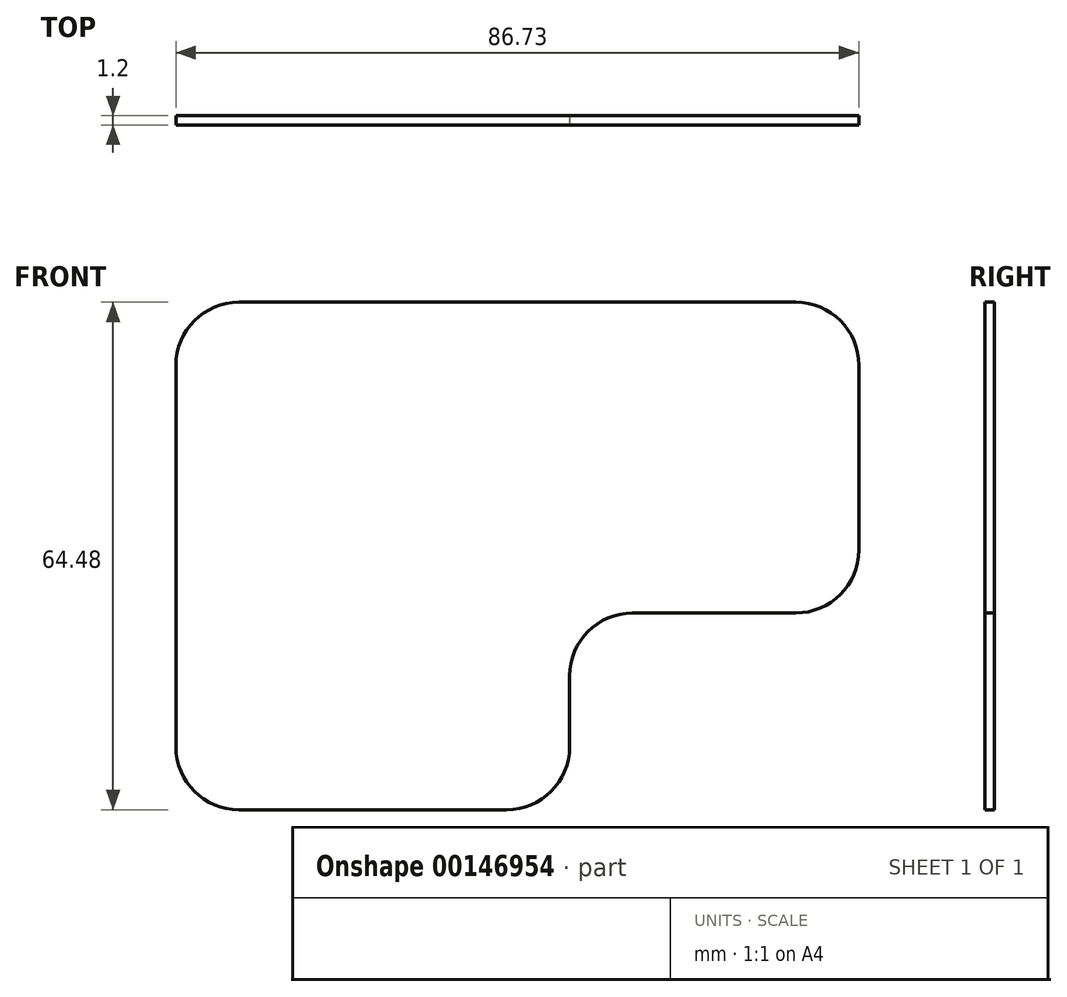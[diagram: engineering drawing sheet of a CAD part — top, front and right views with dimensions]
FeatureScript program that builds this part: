
annotation { "Feature Type Name" : "Feature", "Feature Type Description" : "" }
export const myFeature = defineFeature(function(context is Context, id is Id, definition is map)
    precondition{}
    {
        {
            var Q0;
            Q0=qCreatedBy(makeId("Front.planeOp"),FACE);
            var sketch = newSketch(context, id + "F0", { "sketchPlane" : qUnion([Q0])});
            skLineSegment(sketch, "E0", {"start": v(0, 0) * mm, "end": v(0, 50) * mm, "construction": true});
            skLineSegment(sketch, "E1", {"start": v(0, 50) * mm, "end": v(75, 50) * mm, "construction": true});
            skLineSegment(sketch, "E2", {"start": v(0, 0) * mm, "end": v(30.27, 0) * mm});
            skLineSegment(sketch, "E3", {"start": v(38.27, 8) * mm, "end": v(38.27, 17) * mm});
            skLineSegment(sketch, "E4", {"start": v(46.27, 25) * mm, "end": v(67, 25) * mm});
            skLineSegment(sketch, "E5", {"start": v(75, 33) * mm, "end": v(75, 50) * mm});
            skLineSegment(sketch, "E6", {"start": v(0, 0) * mm, "end": v(-3.73, 0) * mm});
            skLineSegment(sketch, "E7", {"start": v(-11.73, 8) * mm, "end": v(-11.73, 56.48) * mm});
            skLineSegment(sketch, "E8", {"start": v(-3.73, 64.48) * mm, "end": v(67, 64.48) * mm});
            skLineSegment(sketch, "E9", {"start": v(75, 56.48) * mm, "end": v(75, 50) * mm});
            skPoint(sketch, "E10.visualSharp", {"position": v(-11.73, 0) * mm});
            skArc(sketch, "E10.filletArc", {"start": v(-11.73, 8) * mm, "mid": v(-9.39, 2.34) * mm, "end": v(-3.73, 0) * mm});
            skPoint(sketch, "E11.visualSharp", {"position": v(38.27, 0) * mm});
            skArc(sketch, "E11.filletArc", {"start": v(30.27, 0) * mm, "mid": v(35.92, 2.34) * mm, "end": v(38.27, 8) * mm});
            skPoint(sketch, "E12.visualSharp", {"position": v(38.27, 25) * mm});
            skArc(sketch, "E12.filletArc", {"start": v(46.27, 25) * mm, "mid": v(40.61, 22.66) * mm, "end": v(38.27, 17) * mm});
            skPoint(sketch, "E13.visualSharp", {"position": v(-11.73, 64.48) * mm});
            skArc(sketch, "E13.filletArc", {"start": v(-3.73, 64.48) * mm, "mid": v(-9.39, 62.14) * mm, "end": v(-11.73, 56.48) * mm});
            skPoint(sketch, "E14.visualSharp", {"position": v(75, 64.48) * mm});
            skArc(sketch, "E14.filletArc", {"start": v(75, 56.48) * mm, "mid": v(72.66, 62.14) * mm, "end": v(67, 64.48) * mm});
            skPoint(sketch, "E15.visualSharp", {"position": v(75, 25) * mm});
            skArc(sketch, "E15.filletArc", {"start": v(67, 25) * mm, "mid": v(72.66, 27.34) * mm, "end": v(75, 33) * mm});
            skSolve(sketch);
        }
        {
            var Q0;
            Q0 = qSketchRegion(id + "F0", true);
            extrude(context, id + "F1", {"entities" : qUnion([Q0]), "oppositeDirection" : true, "depth" : 1.2 * mm});
        }
    });
